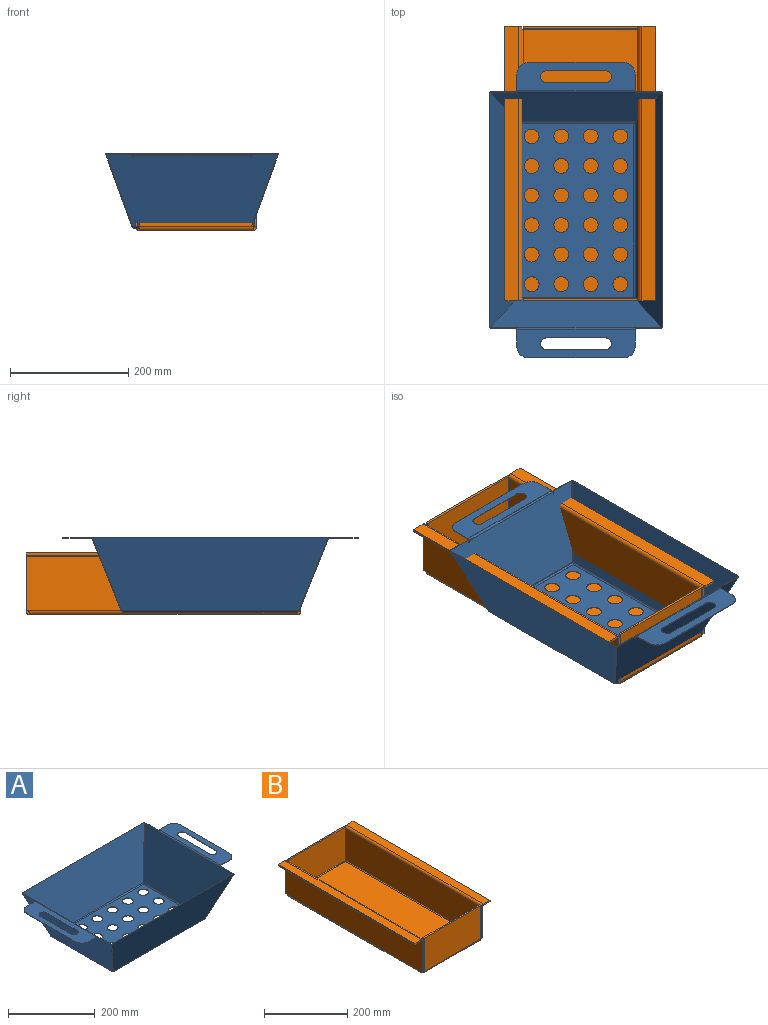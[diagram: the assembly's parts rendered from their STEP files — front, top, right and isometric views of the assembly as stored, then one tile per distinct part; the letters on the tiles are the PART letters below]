
ASSEMBLY  parts=2 mates=1
PART A: 114 faces, bbox 500x292.9x126 mm
  f0: plane 294.58x195.8mm, normal (0,0,1), area 45898.1mm2, adj f1,f2,f3,f4,f5,f6,f7,f8
  f1: cylinder r=12.5mm len=25mm, axis (0,0,1), area 78.5mm2, adj f0,f25
  f2: cylinder r=12.5mm len=25mm, axis (0,0,1), area 78.5mm2, adj f0,f25
  f3: cylinder r=12.5mm len=25mm, axis (0,0,1), area 78.5mm2, adj f0,f25
  f4: cylinder r=12.5mm len=25mm, axis (0,0,1), area 78.5mm2, adj f0,f25
  f5: cylinder r=12.5mm len=25mm, axis (0,0,1), area 78.5mm2, adj f0,f25
  f6: cylinder r=12.5mm len=25mm, axis (0,0,1), area 78.5mm2, adj f0,f25
  f7: cylinder r=12.5mm len=25mm, axis (0,0,1), area 78.5mm2, adj f0,f25
  f8: cylinder r=12.5mm len=25mm, axis (0,0,1), area 78.5mm2, adj f0,f25
  f9: cylinder r=12.5mm len=25mm, axis (0,0,1), area 78.5mm2, adj f0,f25
  f10: cylinder r=12.5mm len=25mm, axis (0,0,1), area 78.5mm2, adj f0,f25
  f11: cylinder r=12.5mm len=25mm, axis (0,0,1), area 78.5mm2, adj f0,f25
  f12: cylinder r=12.5mm len=25mm, axis (0,0,1), area 78.5mm2, adj f0,f25
  f13: cylinder r=12.5mm len=25mm, axis (0,0,1), area 78.5mm2, adj f0,f25
  f14: cylinder r=12.5mm len=25mm, axis (0,0,1), area 78.5mm2, adj f0,f25
  f15: cylinder r=12.5mm len=25mm, axis (0,0,1), area 78.5mm2, adj f0,f25
  f16: cylinder r=12.5mm len=25mm, axis (0,0,1), area 78.5mm2, adj f0,f25
  f17: cylinder r=12.5mm len=25mm, axis (0,0,1), area 78.5mm2, adj f0,f25
  f18: cylinder r=12.5mm len=25mm, axis (0,0,1), area 78.5mm2, adj f0,f25
  f19: cylinder r=12.5mm len=25mm, axis (0,0,1), area 78.5mm2, adj f0,f25
  f20: cylinder r=12.5mm len=25mm, axis (0,0,1), area 78.5mm2, adj f0,f25
  f21: cylinder r=12.5mm len=25mm, axis (0,0,1), area 78.5mm2, adj f0,f25
  f22: cylinder r=12.5mm len=25mm, axis (0,0,1), area 78.5mm2, adj f0,f25
  f23: cylinder r=12.5mm len=25mm, axis (0,0,1), area 78.5mm2, adj f0,f25
  f24: cylinder r=12.5mm len=25mm, axis (0,0,1), area 78.5mm2, adj f0,f25
  f25: plane 294.58x195.8mm, normal (0,0,-1), area 45898.1mm2, adj f1,f2,f3,f4,f5,f6,f7,f8
  f26: plane 1x0.14mm, normal (-0.7,0.72,0), area 0.2mm2, adj f0,f25,f57,f111
  f27: plane 1x0.14mm, normal (-0.7,-0.72,0), area 0.2mm2, adj f0,f25,f58,f99
  f28: plane 1x0.14mm, normal (0.7,-0.72,0), area 0.2mm2, adj f0,f25,f89,f100
  f29: plane 1x0.14mm, normal (0.7,0.72,0), area 0.2mm2, adj f0,f25,f88,f110
  f30: plane 44.02x0.93mm, normal (-0.37,0,0.93), area 44mm2, adj f31,f32,f35,f41
  f31: plane 290.16x122.49mm, normal (0.93,0,0.37), area 31979.3mm2, adj f30,f33,f34,f35,f36,f37,f38,f39
  f32: plane 290.16x122.49mm, normal (-0.93,0,-0.37), area 31979.3mm2, adj f30,f33,f34,f35,f36,f37,f38,f39
  f33: plane 44.02x0.93mm, normal (-0.37,0,0.93), area 44mm2, adj f31,f32,f34,f38
  f34: plane 122.86x49.92mm, normal (0.12,-0.95,-0.3), area 139.3mm2, adj f31,f32,f33,f58
  f35: plane 122.86x49.92mm, normal (0.12,0.95,-0.3), area 139.3mm2, adj f30,f31,f32,f57
  f36: cylinder r=0.53mm len=1.13mm, axis (-0.93,0,-0.37), area 1.7mm2, adj f31,f32,f37,f38
  f37: plane 3.16x2.04mm, normal (0,-1,0), area 3mm2, adj f31,f32,f36,f54
  f38: plane 5.04x2.8mm, normal (0,1,0), area 5mm2, adj f31,f32,f33,f36
  f39: plane 3.16x2.04mm, normal (0,1,0), area 3mm2, adj f31,f32,f40,f53
  f40: cylinder r=0.53mm len=1.13mm, axis (-0.93,0,-0.37), area 1.7mm2, adj f31,f32,f39,f41
  f41: plane 5.04x2.8mm, normal (0,-1,0), area 5mm2, adj f30,f31,f32,f40
  f42: plane 27.97x1mm, normal (0,-1,0), area 28mm2, adj f49,f50,f52,f54
  f43: plane 27.97x1mm, normal (0,1,0), area 28mm2, adj f49,f50,f51,f53
  f44: plane 100x1mm, normal (-1,0,0), area 100mm2, adj f45,f47,f49,f50
  f45: cylinder r=10mm len=20mm, axis (0,0,1), area 31.4mm2, adj f44,f46,f49,f50
  f46: plane 100x1mm, normal (1,0,0), area 100mm2, adj f45,f47,f49,f50
  f47: cylinder r=10mm len=20mm, axis (0,0,1), area 31.4mm2, adj f44,f46,f49,f50
  f48: plane 160x1mm, normal (-1,0,0), area 160mm2, adj f49,f50,f51,f52
  f49: plane 200x47.97mm, normal (0,0,1), area 7107.9mm2, adj f42,f43,f44,f45,f46,f47,f48,f51
  f50: plane 200x47.97mm, normal (0,0,-1), area 7107.9mm2, adj f42,f43,f44,f45,f46,f47,f48,f51
  f51: cylinder r=20mm len=20mm, axis (0,0,-1), area 31.4mm2, adj f43,f48,f49,f50
  f52: cylinder r=20mm len=20mm, axis (0,0,1), area 31.4mm2, adj f42,f48,f49,f50
  f53: plane 3.71x2.89mm, normal (0,1,0), area 4.2mm2, adj f39,f43,f55,f56
  f54: plane 3.71x2.89mm, normal (0,-1,0), area 4.2mm2, adj f37,f42,f55,f56
  f55: cylinder r=4mm len=200mm, axis (0,1,0), area 952.2mm2, adj f31,f49,f53,f54
  f56: cylinder r=3mm len=200mm, axis (0,1,0), area 714.2mm2, adj f32,f50,f53,f54
  f57: bspline ~3.71x2.89mm, area 5mm2, adj f26,f35,f59,f60
  f58: bspline ~3.71x2.89mm, area 5mm2, adj f27,f34,f59,f60
  f59: cylinder r=4mm len=201mm, axis (0,1,0), area 945.9mm2, adj f25,f32,f57,f58
  f60: cylinder r=3mm len=201mm, axis (0,1,0), area 709.4mm2, adj f0,f31,f57,f58
  f61: plane 44.02x0.93mm, normal (0.37,0,0.93), area 44mm2, adj f62,f63,f64,f72
  f62: plane 290.16x122.49mm, normal (-0.93,0,0.37), area 31979.3mm2, adj f61,f64,f65,f66,f67,f68,f69,f70
  f63: plane 290.16x122.49mm, normal (0.93,0,-0.37), area 31979.3mm2, adj f61,f64,f65,f66,f67,f68,f69,f70
  f64: plane 122.86x49.92mm, normal (-0.12,-0.95,-0.3), area 139.3mm2, adj f61,f62,f63,f89
  f65: plane 44.02x0.93mm, normal (0.37,0,0.93), area 44mm2, adj f62,f63,f66,f69
  f66: plane 122.86x49.92mm, normal (-0.12,0.95,-0.3), area 139.3mm2, adj f62,f63,f65,f88
  f67: cylinder r=0.53mm len=1.13mm, axis (0.93,0,-0.37), area 1.7mm2, adj f62,f63,f68,f69
  f68: plane 3.16x2.04mm, normal (0,1,0), area 3mm2, adj f62,f63,f67,f84
  f69: plane 5.04x2.8mm, normal (0,-1,0), area 5mm2, adj f62,f63,f65,f67
  f70: plane 3.16x2.04mm, normal (0,-1,0), area 3mm2, adj f62,f63,f71,f85
  f71: cylinder r=0.53mm len=1.13mm, axis (0.93,0,-0.37), area 1.7mm2, adj f62,f63,f70,f72
  f72: plane 5.04x2.8mm, normal (0,1,0), area 5mm2, adj f61,f62,f63,f71
  f73: cylinder r=10mm len=20mm, axis (0,0,1), area 31.4mm2, adj f74,f79,f80,f81
  f74: plane 100x1mm, normal (1,0,0), area 100mm2, adj f73,f75,f80,f81
  f75: cylinder r=10mm len=20mm, axis (0,0,1), area 31.4mm2, adj f74,f79,f80,f81
  f76: plane 27.97x1mm, normal (0,-1,0), area 28mm2, adj f80,f81,f82,f85
  f77: plane 160x1mm, normal (1,0,0), area 160mm2, adj f80,f81,f82,f83
  f78: plane 27.97x1mm, normal (0,1,0), area 28mm2, adj f80,f81,f83,f84
  f79: plane 100x1mm, normal (-1,0,0), area 100mm2, adj f73,f75,f80,f81
  f80: plane 200x47.97mm, normal (0,0,1), area 7107.9mm2, adj f73,f74,f75,f76,f77,f78,f79,f82
  f81: plane 200x47.97mm, normal (0,0,-1), area 7107.9mm2, adj f73,f74,f75,f76,f77,f78,f79,f82
  f82: cylinder r=20mm len=20mm, axis (0,0,1), area 31.4mm2, adj f76,f77,f80,f81
  f83: cylinder r=20mm len=20mm, axis (0,0,-1), area 31.4mm2, adj f77,f78,f80,f81
  f84: plane 3.71x2.89mm, normal (0,1,0), area 4.2mm2, adj f68,f78,f86,f87
  f85: plane 3.71x2.89mm, normal (0,-1,0), area 4.2mm2, adj f70,f76,f86,f87
  f86: cylinder r=4mm len=200mm, axis (0,1,0), area 952.2mm2, adj f62,f80,f84,f85
  f87: cylinder r=3mm len=200mm, axis (0,1,0), area 714.2mm2, adj f63,f81,f84,f85
  f88: bspline ~3.71x2.89mm, area 5mm2, adj f29,f66,f90,f91
  f89: bspline ~3.71x2.89mm, area 5mm2, adj f28,f64,f90,f91
  f90: cylinder r=4mm len=201mm, axis (0,1,0), area 946mm2, adj f25,f63,f88,f89
  f91: cylinder r=3mm len=201mm, axis (0,1,0), area 709.4mm2, adj f0,f62,f88,f89
  f92: plane 1.05x0.65mm, normal (-0.94,0.12,-0.33), area 0.4mm2, adj f93,f96,f97,f98
  f93: plane 398.27x0.94mm, normal (0,-0.34,0.94), area 398.3mm2, adj f92,f94,f97,f98
  f94: plane 1.05x0.65mm, normal (0.94,0.12,-0.33), area 0.4mm2, adj f93,f95,f97,f98
  f95: plane 123.06x49.09mm, normal (0.94,0.12,-0.33), area 139.5mm2, adj f94,f97,f98,f100
  f96: plane 123.06x49.09mm, normal (-0.94,0.12,-0.33), area 139.5mm2, adj f92,f97,f98,f99
  f97: plane 398.27x123.03mm, normal (0,0.94,0.34), area 45699mm2, adj f92,f93,f94,f95,f96,f102
  f98: plane 398.27x123.03mm, normal (0,-0.94,-0.34), area 45699mm2, adj f92,f93,f94,f95,f96,f101
  f99: bspline ~3.76x2.97mm, area 5.2mm2, adj f27,f96,f101,f102
  f100: bspline ~3.76x2.97mm, area 5.1mm2, adj f28,f95,f101,f102
  f101: cylinder r=4mm len=299.85mm, axis (-1,0,0), area 1453.6mm2, adj f25,f98,f99,f100
  f102: cylinder r=3mm len=299.85mm, axis (-1,0,0), area 1090.2mm2, adj f0,f97,f99,f100
  f103: plane 1.05x0.65mm, normal (0.94,-0.12,-0.33), area 0.4mm2, adj f104,f107,f108,f109
  f104: plane 398.27x0.94mm, normal (0,0.34,0.94), area 398.3mm2, adj f103,f105,f108,f109
  f105: plane 1.05x0.65mm, normal (-0.94,-0.12,-0.33), area 0.4mm2, adj f104,f106,f108,f109
  f106: plane 123.06x49.09mm, normal (-0.94,-0.12,-0.33), area 139.5mm2, adj f105,f108,f109,f111
  f107: plane 123.06x49.09mm, normal (0.94,-0.12,-0.33), area 139.5mm2, adj f103,f108,f109,f110
  f108: plane 398.27x123.03mm, normal (0,-0.94,0.34), area 45699mm2, adj f103,f104,f105,f106,f107,f113
  f109: plane 398.27x123.03mm, normal (0,0.94,-0.34), area 45699mm2, adj f103,f104,f105,f106,f107,f112
  f110: bspline ~3.76x2.97mm, area 5.2mm2, adj f29,f107,f112,f113
  f111: bspline ~3.76x2.97mm, area 5.1mm2, adj f26,f106,f112,f113
  f112: cylinder r=4mm len=299.85mm, axis (1,0,0), area 1453.6mm2, adj f25,f109,f110,f111
  f113: cylinder r=3mm len=299.85mm, axis (1,0,0), area 1090.2mm2, adj f0,f108,f110,f111
PART B: 58 faces, bbox 255x465x104 mm
  f0: plane 453x193mm, normal (0,0,-1), area 87429mm2, adj f9,f18,f22,f26
  f1: plane 453x193mm, normal (0,0,1), area 87429mm2, adj f10,f19,f23,f27
  f2: plane 193x4mm, normal (0,0,1), area 772mm2, adj f3,f4,f5,f6
  f3: plane 98x4mm, normal (1,0,0), area 392mm2, adj f2,f5,f6,f7
  f4: plane 98x4mm, normal (-1,0,0), area 392mm2, adj f2,f5,f6,f8
  f5: plane 193x98mm, normal (0,1,0), area 18914mm2, adj f2,f3,f4,f9
  f6: plane 193x98mm, normal (0,-1,0), area 18914mm2, adj f2,f3,f4,f10
  f7: plane 6x6mm, normal (1,0,0), area 25.1mm2, adj f3,f9,f10,f20
  f8: plane 6x6mm, normal (-1,0,0), area 25.1mm2, adj f4,f9,f10,f24
  f9: cylinder r=6mm len=193mm, axis (1,0,0), area 1819mm2, adj f0,f5,f7,f8
  f10: cylinder r=2mm len=193mm, axis (1,0,0), area 606.3mm2, adj f1,f6,f7,f8
  f11: plane 193x4mm, normal (0,0,1), area 772mm2, adj f12,f13,f14,f15
  f12: plane 98x4mm, normal (-1,0,0), area 392mm2, adj f11,f14,f15,f16
  f13: plane 98x4mm, normal (1,0,0), area 392mm2, adj f11,f14,f15,f17
  f14: plane 193x98mm, normal (0,-1,0), area 18914mm2, adj f11,f12,f13,f18
  f15: plane 193x98mm, normal (0,1,0), area 18914mm2, adj f11,f12,f13,f19
  f16: plane 6x6mm, normal (-1,0,0), area 25.1mm2, adj f12,f18,f19,f25
  f17: plane 6x6mm, normal (1,0,0), area 25.1mm2, adj f13,f18,f19,f21
  f18: cylinder r=6mm len=193mm, axis (-1,0,0), area 1819mm2, adj f0,f14,f16,f17
  f19: cylinder r=2mm len=193mm, axis (-1,0,0), area 606.3mm2, adj f1,f15,f16,f17
  f20: plane 6x6mm, normal (0,1,0), area 25.1mm2, adj f7,f22,f23,f45
  f21: plane 6x6mm, normal (0,-1,0), area 25.1mm2, adj f17,f22,f23,f43
  f22: cylinder r=6mm len=453mm, axis (0,1,0), area 4269.4mm2, adj f0,f20,f21,f47
  f23: cylinder r=2mm len=453mm, axis (0,1,0), area 1423.1mm2, adj f1,f20,f21,f48
  f24: plane 6x6mm, normal (0,1,0), area 25.1mm2, adj f8,f26,f27,f28
  f25: plane 6x6mm, normal (0,-1,0), area 25.1mm2, adj f16,f26,f27,f31
  f26: cylinder r=6mm len=453mm, axis (0,1,0), area 4269.4mm2, adj f0,f24,f25,f32
  f27: cylinder r=2mm len=453mm, axis (0,1,0), area 1423.1mm2, adj f1,f24,f25,f33
  f28: plane 6x4mm, normal (0,0,-1), area 24mm2, adj f24,f30,f32,f33
  f29: plane 92x4mm, normal (0,-1,0), area 368mm2, adj f31,f32,f33,f40
  f30: plane 92x4mm, normal (0,1,0), area 368mm2, adj f28,f32,f33,f39
  f31: plane 6x4mm, normal (0,0,-1), area 24mm2, adj f25,f29,f32,f33
  f32: plane 465x92mm, normal (-1,0,0), area 42780mm2, adj f26,f28,f29,f30,f31,f42
  f33: plane 465x92mm, normal (1,0,0), area 42780mm2, adj f27,f28,f29,f30,f31,f41
  f34: plane 23x4mm, normal (0,-1,0), area 92mm2, adj f35,f37,f38,f40
  f35: plane 465x4mm, normal (-1,0,0), area 1860mm2, adj f34,f36,f37,f38
  f36: plane 23x4mm, normal (0,1,0), area 92mm2, adj f35,f37,f38,f39
  f37: plane 465x23mm, normal (0,0,-1), area 10695mm2, adj f34,f35,f36,f42
  f38: plane 465x23mm, normal (0,0,1), area 10695mm2, adj f34,f35,f36,f41
  f39: plane 6x6mm, normal (0,1,0), area 25.1mm2, adj f30,f36,f41,f42
  f40: plane 6x6mm, normal (0,-1,0), area 25.1mm2, adj f29,f34,f41,f42
  f41: cylinder r=6mm len=465mm, axis (0,1,0), area 4382.5mm2, adj f33,f38,f39,f40
  f42: cylinder r=2mm len=465mm, axis (0,1,0), area 1460.8mm2, adj f32,f37,f39,f40
  f43: plane 6x4mm, normal (0,0,-1), area 24mm2, adj f21,f44,f47,f48
  f44: plane 92x4mm, normal (0,-1,0), area 368mm2, adj f43,f47,f48,f55
  f45: plane 6x4mm, normal (0,0,-1), area 24mm2, adj f20,f46,f47,f48
  f46: plane 92x4mm, normal (0,1,0), area 368mm2, adj f45,f47,f48,f54
  f47: plane 465x92mm, normal (1,0,0), area 42780mm2, adj f22,f43,f44,f45,f46,f57
  f48: plane 465x92mm, normal (-1,0,0), area 42780mm2, adj f23,f43,f44,f45,f46,f56
  f49: plane 23x4mm, normal (0,-1,0), area 92mm2, adj f51,f52,f53,f55
  f50: plane 23x4mm, normal (0,1,0), area 92mm2, adj f51,f52,f53,f54
  f51: plane 465x4mm, normal (1,0,0), area 1860mm2, adj f49,f50,f52,f53
  f52: plane 465x23mm, normal (0,0,-1), area 10695mm2, adj f49,f50,f51,f57
  f53: plane 465x23mm, normal (0,0,1), area 10695mm2, adj f49,f50,f51,f56
  f54: plane 6x6mm, normal (0,1,0), area 25.1mm2, adj f46,f50,f56,f57
  f55: plane 6x6mm, normal (0,-1,0), area 25.1mm2, adj f44,f49,f56,f57
  f56: cylinder r=6mm len=465mm, axis (0,1,0), area 4382.5mm2, adj f48,f53,f54,f55
  f57: cylinder r=2mm len=465mm, axis (0,1,0), area 1460.8mm2, adj f47,f52,f54,f55
PLACE A rot(axis=(0,0,-1),90deg) t=(-105.2,-78.5,-82.26)mm
PLACE B t=(1.93,-231.95,-36.26)mm
MATE planar A.f25 <-> B.f1  axis (0,0,-1) through (-5.2,-78.5,-82.26)mm
